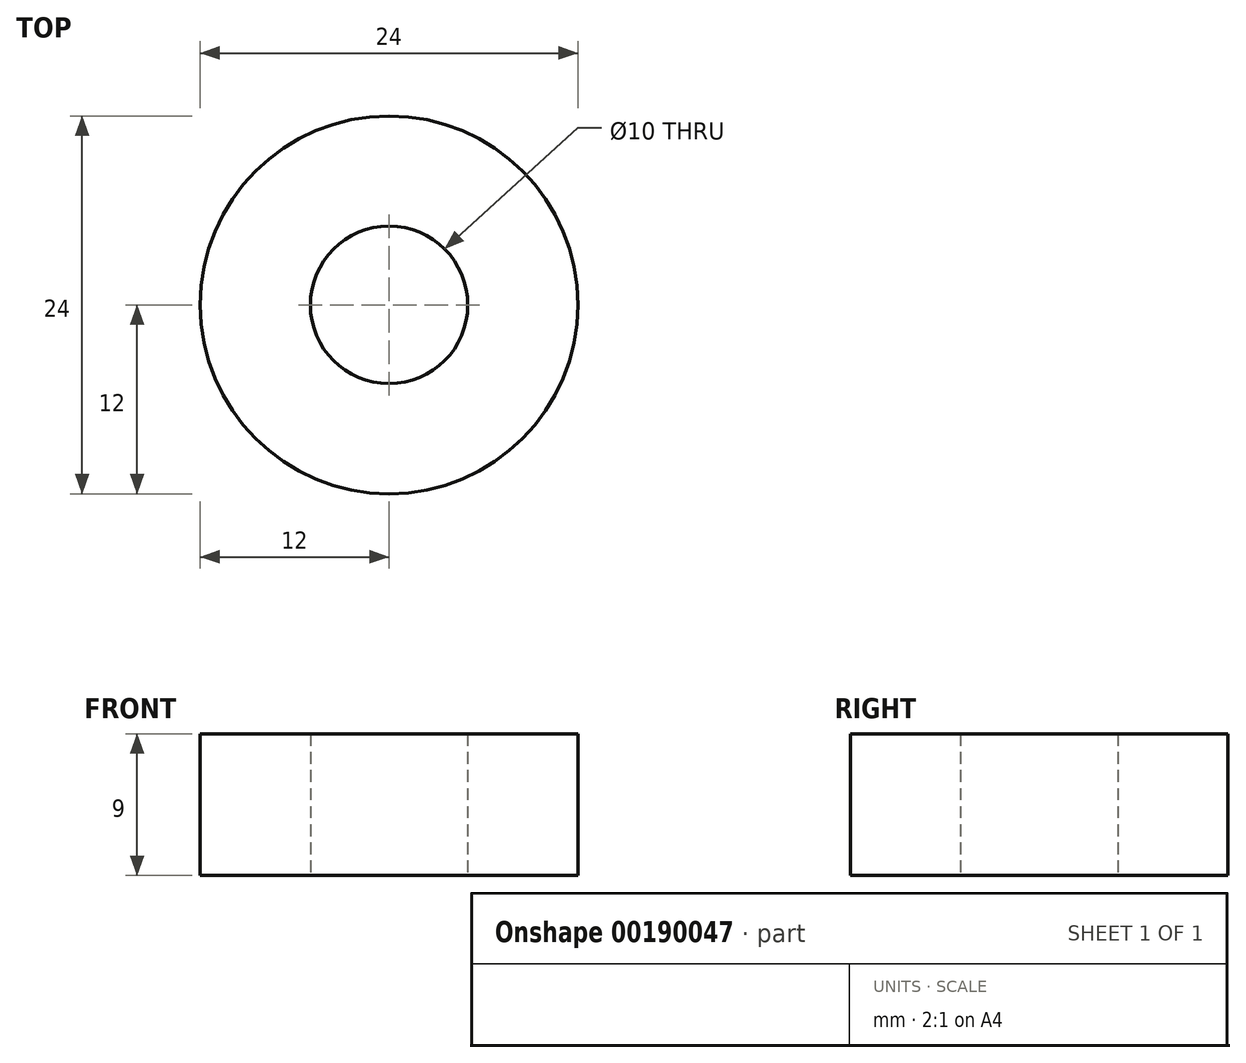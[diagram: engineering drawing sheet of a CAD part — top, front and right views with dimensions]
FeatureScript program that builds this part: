
annotation { "Feature Type Name" : "Feature", "Feature Type Description" : "" }
export const myFeature = defineFeature(function(context is Context, id is Id, definition is map)
    precondition{}
    {
        {
            var Q0;
            Q0=qCreatedBy(makeId("Top.planeOp"),FACE);
            var sketch = newSketch(context, id + "F0", { "sketchPlane" : qUnion([Q0])});
            skCircle(sketch, "E0", {"center": v(0, 0) * mm, "radius": 12 * mm});
            skCircle(sketch, "E1", {"center": v(0, 0) * mm, "radius": 5 * mm});
            skSolve(sketch);
        }
        {
            var Q0;
            Q0=makeQuery(id+"F0.imprint","IMPRINT",FACE,{"disambiguationData":[TD([[makeQuery(id+"F0.imprint","IMPRINT",EDGE,{"derivedFrom":sQuery(id+"F0.wireOp",EDGE,"E0")}),1.0]])]});
            extrude(context, id + "F1", {"entities" : qUnion([Q0]), "depth" : 9 * mm});
        }
    });
